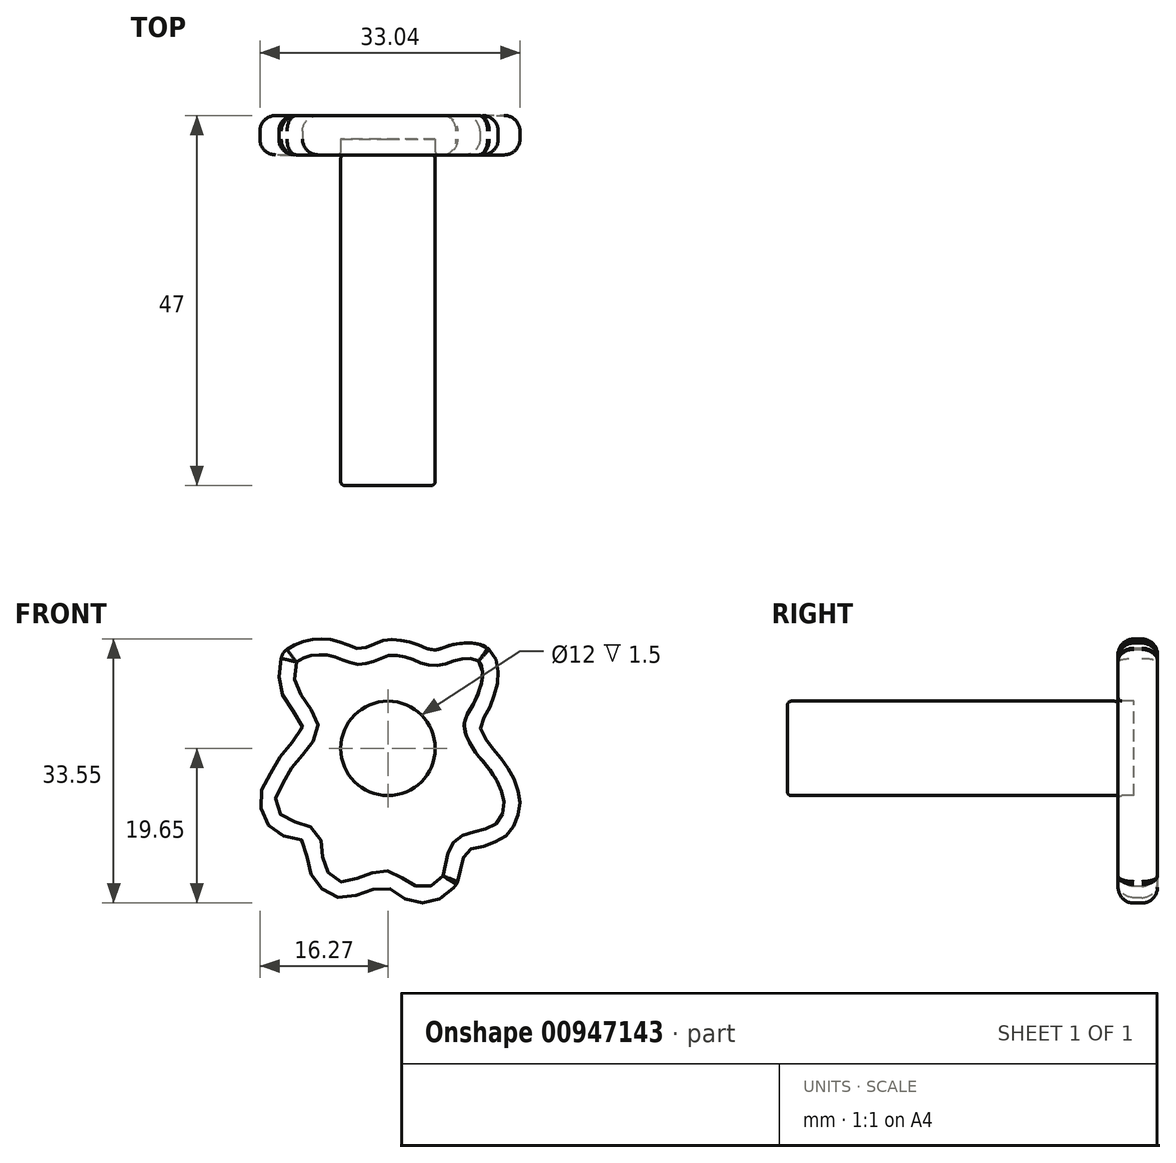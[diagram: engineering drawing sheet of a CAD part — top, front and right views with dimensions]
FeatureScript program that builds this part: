
annotation { "Feature Type Name" : "Feature", "Feature Type Description" : "" }
export const myFeature = defineFeature(function(context is Context, id is Id, definition is map)
    precondition{}
    {
        {
            var Q0;
            Q0=qCreatedBy(makeId("Front.planeOp"),FACE);
            var sketch = newSketch(context, id + "F0", { "sketchPlane" : qUnion([Q0])});
            skCircle(sketch, "E0", {"center": v(0, 0) * mm, "radius": 6 * mm});
            skPoint(sketch, "E1.55.internal.snap0", {"position": v(58.6, -3.2) * mm});
            skFitSpline(sketch, "E2", {"points": [v(-6.39, 13.6) * mm, v(-7.22, 13.82) * mm, v(-8.35, 13.9) * mm, v(-9.34, 13.86) * mm, v(-10.4, 13.7) * mm, v(-11.12, 13.48) * mm, v(-12, 13.1) * mm, v(-12.72, 12.63) * mm, v(-13.29, 12.12) * mm, v(-13.55, 11.48) * mm, v(-13.73, 10.42) * mm, v(-13.85, 8.5) * mm, v(-13.7, 7.47) * mm, v(-13.23, 6.5) * mm, v(-11.24, 3.62) * mm, v(-10.86, 2.83) * mm, v(-11.08, 2.17) * mm, v(-11.49, 1.54) * mm, v(-12.38, 0.47) * mm, v(-14.34, -1.98) * mm, v(-15.02, -3.34) * mm, v(-15.86, -4.72) * mm, v(-16.27, -6.73) * mm, v(-15.88, -8.39) * mm, v(-15.4, -9.4) * mm, v(-14.81, -10.17) * mm, v(-14.22, -10.7) * mm, v(-13.1, -11.17) * mm, v(-12.12, -11.32) * mm, v(-11.31, -11.44) * mm, v(-10.9, -11.67) * mm, v(-10.54, -12.06) * mm, v(-10.34, -12.63) * mm, v(-10.27, -13.9) * mm, v(-10.13, -15.05) * mm, v(-9.96, -15.61) * mm, v(-9.53, -16.45) * mm, v(-8.9, -17.34) * mm, v(-8.09, -18.08) * mm, v(-7.3, -18.56) * mm, v(-6.99, -18.7) * mm, v(-6.44, -18.9) * mm, v(-5.62, -18.96) * mm, v(-4.38, -18.78) * mm, v(-3, -18.32) * mm, v(-2.1, -17.98) * mm, v(-1.17, -17.62) * mm, v(-0.72, -17.52) * mm, v(-0.32, -17.55) * mm, v(-0.04, -17.67) * mm, v(0.47, -17.96) * mm, v(0.72, -18.16) * mm, v(1.35, -18.63) * mm, v(2.29, -19.16) * mm, v(3.04, -19.41) * mm, v(3.88, -19.6) * mm, v(4.8, -19.63) * mm, v(5.93, -19.42) * mm, v(6.84, -19.01) * mm, v(7.61, -18.5) * mm, v(8.26, -17.8) * mm, v(8.8, -17.03) * mm, v(9.18, -15.5) * mm, v(9.56, -13.9) * mm, v(9.93, -13.09) * mm, v(10.83, -12.68) * mm, v(12, -12.46) * mm, v(13.71, -11.81) * mm, v(14.99, -11.15) * mm, v(15.86, -10.06) * mm, v(16.43, -8.88) * mm, v(16.76, -7.08) * mm, v(16.73, -6.24) * mm, v(16.4, -5.07) * mm, v(15.95, -3.8) * mm, v(15.25, -2.56) * mm, v(14.27, -1.17) * mm, v(12.75, 0.69) * mm, v(12, 1.87) * mm, v(11.7, 2.7) * mm, v(11.73, 3.15) * mm, v(12, 3.64) * mm, v(12.72, 4.82) * mm, v(13.47, 6.62) * mm, v(13.87, 8.13) * mm, v(14.01, 9.44) * mm, v(13.8, 11.15) * mm, v(13.3, 12.06) * mm, v(12.74, 12.67) * mm, v(11.94, 13.1) * mm, v(11.1, 13.34) * mm, v(10.25, 13.4) * mm, v(9.36, 13.34) * mm, v(8.42, 13.2) * mm, v(7.58, 13) * mm, v(6.94, 12.75) * mm, v(6.35, 12.57) * mm, v(5.74, 12.53) * mm, v(5.03, 12.66) * mm, v(3.95, 13.12) * mm, v(2.97, 13.45) * mm, v(2.04, 13.67) * mm, v(0.8, 13.83) * mm, v(-0.46, 13.75) * mm, v(-1.7, 13.27) * mm, v(-3, 12.78) * mm, v(-3.79, 12.69) * mm, v(-5.08, 13.14) * mm, v(-6.39, 13.6) * mm]});
            skSolve(sketch);
        }
        {
            var Q0;
            Q0=makeQuery(id+"F0.imprint","IMPRINT",FACE,{"disambiguationData":[TD([[makeQuery(id+"F0.imprint","IMPRINT",EDGE,{"derivedFrom":sQuery(id+"F0.wireOp",EDGE,"E2")}),1.0]])]});
            extrude(context, id + "F1", {"entities" : qUnion([Q0]), "oppositeDirection" : true, "depth" : 5 * mm, "offsetDistance" : 25 * mm});
        }
        {
            var Q0;
            Q0=makeQuery(id+"F0.imprint","IMPRINT",FACE,{"disambiguationData":[TD([[makeQuery(id+"F0.imprint","IMPRINT",EDGE,{"derivedFrom":sQuery(id+"F0.wireOp",EDGE,"E0")}),1.0]])]});
            extrude(context, id + "F2", {"entities" : qUnion([Q0]), "operationType" : NewBodyOperationType.ADD, "oppositeDirection" : true, "depth" : 5 * mm, "offsetDistance" : 25 * mm, "hasSecondDirection" : true, "secondDirectionOppositeDirection" : true, "secondDirectionDepth" : 2 * mm});
        }
        {
            var Q0;
            Q0=makeQuery(id+"F0.imprint","IMPRINT",FACE,{"disambiguationData":[TD([[makeQuery(id+"F0.imprint","IMPRINT",EDGE,{"derivedFrom":sQuery(id+"F0.wireOp",EDGE,"E0")}),1.0]])]});
            extrude(context, id + "F3", {"entities" : qUnion([Q0]), "depth" : 42 * mm, "offsetDistance" : 25 * mm});
        }
        {
            var Q0;
            Q0=makeQuery(id+"F3.opExtrude","CAP_EDGE",EDGE,{"disambiguationData":[OSD([sQuery(id+"F0.wireOp",EDGE,"E0")])],"isStart":false});
            var Q1;
            Q1=makeQuery(id+"F3.opExtrude","CAP_EDGE",EDGE,{"disambiguationData":[OSD([sQuery(id+"F0.wireOp",EDGE,"E0")])],"isStart":true});
            fillet(context, id + "F4", {"entities" : qUnion([Q0, Q1]), "radius" : 0.5 * mm, "tangentPropagation" : true, "allowEdgeOverflow" : false});
        }
        {
            var Q0;
            Q0=makeQuery(id+"F2.opExtrude","CAP_EDGE",EDGE,{"disambiguationData":[OSD([sQuery(id+"F0.wireOp",EDGE,"E0")])],"isStart":true});
            var Q1;
            Q1=makeQuery(id+"F1.opExtrude","CAP_EDGE",EDGE,{"disambiguationData":[OSD([sQuery(id+"F0.wireOp",EDGE,"E0")])],"isStart":true});
            fillet(context, id + "F5", {"entities" : qUnion([Q0, Q1]), "radius" : 0.5 * mm, "tangentPropagation" : true, "allowEdgeOverflow" : false});
        }
        {
            var Q0;
            Q0=makeQuery(id+"F1.opExtrude","CAP_EDGE",EDGE,{"disambiguationData":[OSD([sQuery(id+"F0.wireOp",EDGE,"E2")])],"isStart":true});
            var Q1;
            Q1=makeQuery(id+"F1.opExtrude","CAP_EDGE",EDGE,{"disambiguationData":[OSD([sQuery(id+"F0.wireOp",EDGE,"E2")])],"isStart":false});
            fillet(context, id + "F6", {"entities" : qUnion([Q0, Q1]), "radius" : 2 * mm, "tangentPropagation" : true, "allowEdgeOverflow" : false});
        }
    });
